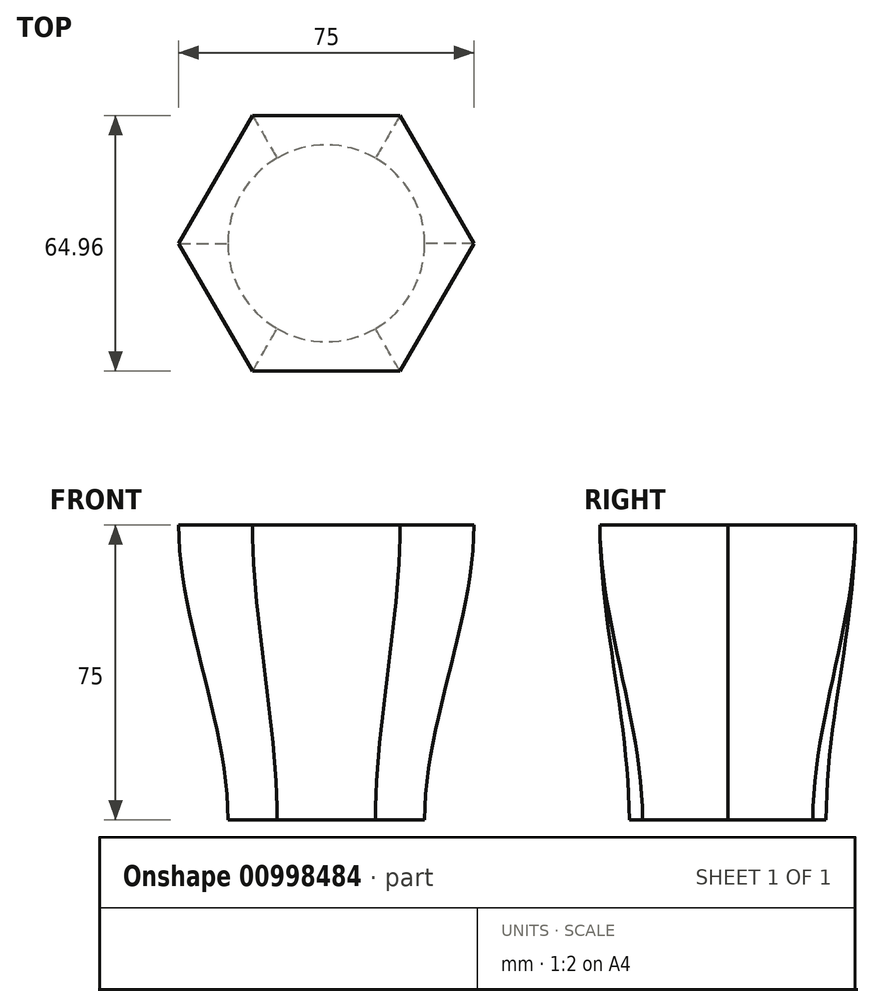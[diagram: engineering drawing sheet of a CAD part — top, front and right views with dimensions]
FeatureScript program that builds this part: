
annotation { "Feature Type Name" : "Feature", "Feature Type Description" : "" }
export const myFeature = defineFeature(function(context is Context, id is Id, definition is map)
    precondition{}
    {
        {
            var Q0;
            Q0=qCreatedBy(makeId("Top.planeOp"),FACE);
            var sketch = newSketch(context, id + "F0", { "sketchPlane" : qUnion([Q0])});
            skCircle(sketch, "E0", {"center": v(0, 0) * mm, "radius": 25 * mm});
            skSolve(sketch);
        }
        {
            var Q0;
            Q0=qCreatedBy(makeId("Top.planeOp"),FACE);
            cPlane(context, id + "F1", {"entities" : qUnion([Q0]), "cplaneType" : CPlaneType.OFFSET, "offset" : 75 * mm, "width" : 150 * mm, "height" : 150 * mm});
        }
        {
            var Q0;
            Q0=qCreatedBy(id+"F1.planeOp",FACE);
            var sketch = newSketch(context, id + "F2", { "sketchPlane" : qUnion([Q0])});
            skCircle(sketch, "E1.cCircle", {"center": v(0, 0) * mm, "radius": 37.5 * mm, "construction": true});
            skLineSegment(sketch, "E1.0", {"start": v(-18.75, 32.48) * mm, "end": v(18.75, 32.48) * mm});
            skLineSegment(sketch, "E1.1", {"start": v(18.75, 32.48) * mm, "end": v(37.5, 0) * mm});
            skLineSegment(sketch, "E1.2", {"start": v(37.5, 0) * mm, "end": v(18.75, -32.48) * mm});
            skLineSegment(sketch, "E1.3", {"start": v(18.75, -32.48) * mm, "end": v(-18.75, -32.48) * mm});
            skLineSegment(sketch, "E1.4", {"start": v(-18.75, -32.48) * mm, "end": v(-37.5, 0) * mm});
            skLineSegment(sketch, "E1.5", {"start": v(-37.5, 0) * mm, "end": v(-18.75, 32.48) * mm});
            skSolve(sketch);
        }
        {
            var Q0;
            Q0=makeQuery(id+"F2.imprint","IMPRINT",FACE,{"disambiguationData":[TD([[makeQuery(id+"F2.imprint","IMPRINT",EDGE,{"derivedFrom":sQuery(id+"F2.wireOp",EDGE,"E1.0")}),-1.0]])]});
            var Q1;
            Q1=makeQuery(id+"F0.imprint","IMPRINT",FACE,{"disambiguationData":[TD([[makeQuery(id+"F0.imprint","IMPRINT",EDGE,{"derivedFrom":sQuery(id+"F0.wireOp",EDGE,"E0")}),1.0]])]});
            loft(context, id + "F3", {"startCondition" : LoftEndDerivativeType.NORMAL_TO_PROFILE, "startMagnitude" : 1, "endCondition" : LoftEndDerivativeType.NORMAL_TO_PROFILE, "endMagnitude" : 1, "sheetProfilesArray" : [{ "sheetProfileEntities" : qUnion([Q0]) }, { "sheetProfileEntities" : qUnion([Q1]) }]});
        }
    });
